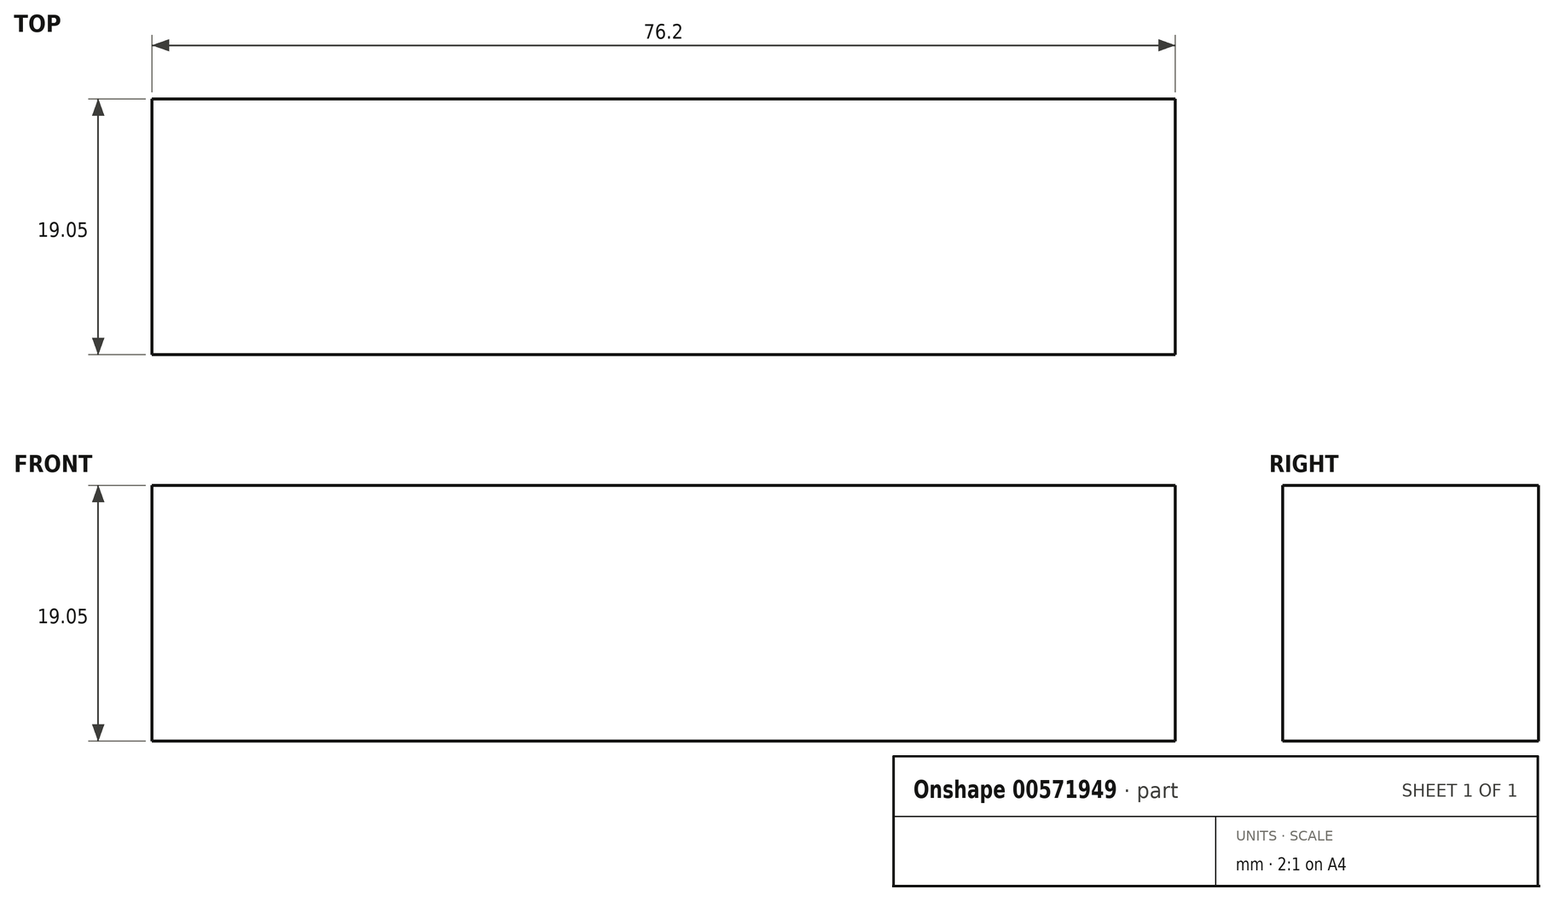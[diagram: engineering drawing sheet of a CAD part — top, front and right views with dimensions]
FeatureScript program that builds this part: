
annotation { "Feature Type Name" : "Feature", "Feature Type Description" : "" }
export const myFeature = defineFeature(function(context is Context, id is Id, definition is map)
    precondition{}
    {
        {
            var Q0;
            Q0=qCreatedBy(makeId("Top.planeOp"),FACE);
            var sketch = newSketch(context, id + "F0", { "sketchPlane" : qUnion([Q0])});
            skLineSegment(sketch, "E0.bottom", {"start": v(0, 0) * mm, "end": v(-76.2, 0) * mm});
            skLineSegment(sketch, "E0.top", {"start": v(0, -19.05) * mm, "end": v(-76.2, -19.05) * mm});
            skLineSegment(sketch, "E0.left", {"start": v(0, 0) * mm, "end": v(0, -19.05) * mm});
            skLineSegment(sketch, "E0.right", {"start": v(-76.2, 0) * mm, "end": v(-76.2, -19.05) * mm});
            skSolve(sketch);
        }
        {
            var Q0;
            Q0 = qSketchRegion(id + "F0", true);
            extrude(context, id + "F1", {"entities" : qUnion([Q0]), "depth" : 19.05 * mm, "offsetDistance" : 25.4 * mm});
        }
    });
